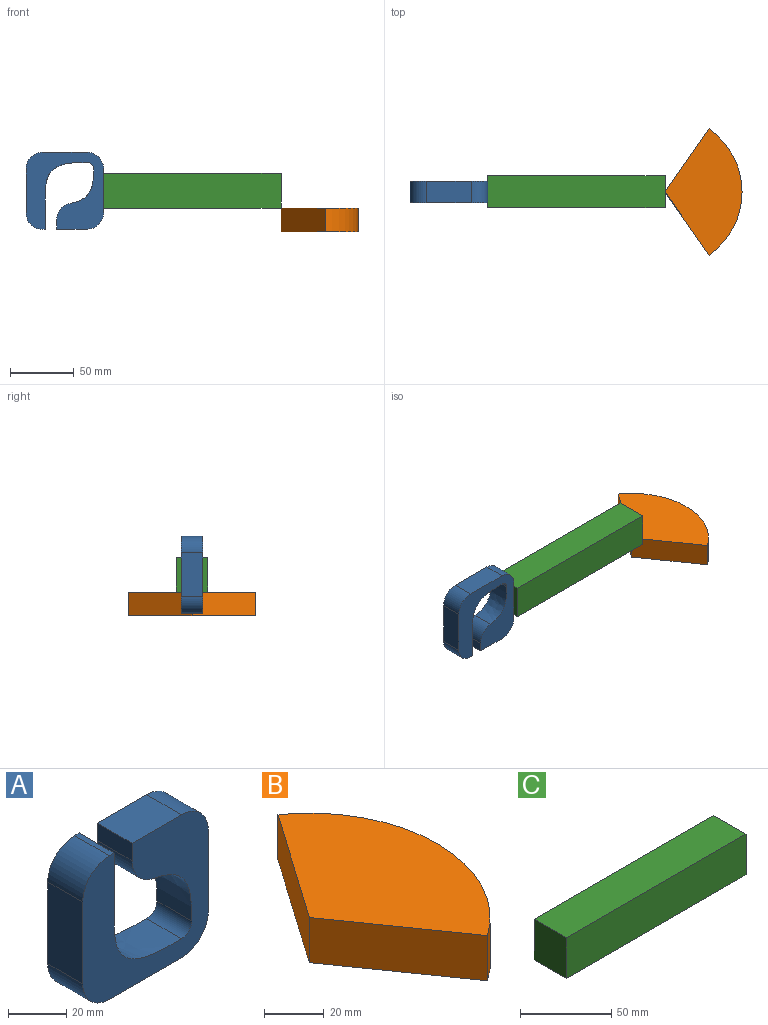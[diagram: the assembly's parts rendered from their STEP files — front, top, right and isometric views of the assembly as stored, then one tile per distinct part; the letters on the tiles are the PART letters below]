
ASSEMBLY  parts=3 mates=2
PART A: 17 faces, bbox 61.1x17x60.5 mm
  f0: extruded ~32.78x22.25mm, area 787mm2, adj f1,f10,f11,f12
  f1: plane 30.25x17mm, normal (1,0,0), area 514.2mm2, adj f0,f2,f11,f12
  f2: plane 17x2.28mm, normal (0,0,1), area 38.7mm2, adj f1,f11,f12,f13
  f3: plane 34.49x17mm, normal (-1,0,0), area 586.3mm2, adj f11,f12,f13,f14
  f4: plane 35.06x17mm, normal (0,0,-1), area 596mm2, adj f5,f11,f12,f14
  f5: cylinder r=13mm len=17mm, axis (0,1,0), area 347.1mm2, adj f4,f6,f11,f12
  f6: plane 34.24x17mm, normal (1,0,0), area 582.1mm2, adj f5,f11,f12,f15
  f7: plane 24x17mm, normal (0,0,1), area 408mm2, adj f8,f11,f12,f15
  f8: plane 17x7.36mm, normal (-1,0,0), area 125.1mm2, adj f7,f11,f12,f16
  f9: extruded ~27.07x18.18mm, area 626mm2, adj f10,f11,f12,f16
  f10: cylinder r=5mm len=17mm, axis (0,1,0), area 133.5mm2, adj f0,f9,f11,f12
  f11: plane 61.06x60.49mm, normal (0,-1,0), area 2294.6mm2, adj f0,f1,f2,f3,f4,f5,f6,f7
  f12: plane 61.06x60.49mm, normal (0,1,0), area 2294.6mm2, adj f0,f1,f2,f3,f4,f5,f6,f7
  f13: cylinder r=13mm len=17mm, axis (0,-1,0), area 347.1mm2, adj f2,f3,f11,f12
  f14: cylinder r=13mm len=17mm, axis (0,1,0), area 347.1mm2, adj f3,f4,f11,f12
  f15: cylinder r=13mm len=17mm, axis (0,1,0), area 347.1mm2, adj f6,f7,f11,f12
  f16: cylinder r=13mm len=17mm, axis (0,1,0), area 309.9mm2, adj f8,f9,f11,f12
PART B: 5 faces, bbox 60.4x99x18.5 mm
  f0: plane 98.98x60.42mm, normal (0,0,-1), area 3503.9mm2, adj f1,f3,f4
  f1: cylinder r=60.42mm len=98.98mm, axis (0,0,-1), area 2142.5mm2, adj f0,f2,f3,f4
  f2: plane 98.98x60.42mm, normal (0,0,1), area 3503.9mm2, adj f1,f3,f4
  f3: plane 49.49x34.65mm, normal (-0.82,0.57,0), area 1116mm2, adj f0,f1,f2,f4
  f4: plane 49.49x34.65mm, normal (-0.82,-0.57,0), area 1116mm2, adj f0,f1,f2,f3
PART C: 6 faces, bbox 139.1x25x27.3 mm
  f0: plane 139.11x25mm, normal (0,0,-1), area 3477.8mm2, adj f1,f3,f4,f5
  f1: plane 27.32x25mm, normal (1,0,0), area 683mm2, adj f0,f2,f4,f5
  f2: plane 139.11x25mm, normal (0,0,1), area 3477.8mm2, adj f1,f3,f4,f5
  f3: plane 27.32x25mm, normal (-1,0,0), area 683mm2, adj f0,f2,f4,f5
  f4: plane 139.11x27.32mm, normal (0,-1,0), area 3800.8mm2, adj f0,f1,f2,f3
  f5: plane 139.11x27.32mm, normal (0,1,0), area 3800.8mm2, adj f0,f1,f2,f3
PLACE A rot(axis=(1,0,0),180deg) t=(-148.74,0.26,10.08)mm
PLACE B t=(-18.46,0.26,-82.73)mm
PLACE C t=(-25.77,0.26,10.2)mm
MATE revolute B.f1 <-> C.f0  axis (0,0,1) through (43.78,0.26,-3.46)mm
MATE fastened A.f6 <-> C.f3  axis (1,0,0) through (-95.33,0.26,10.2)mm
